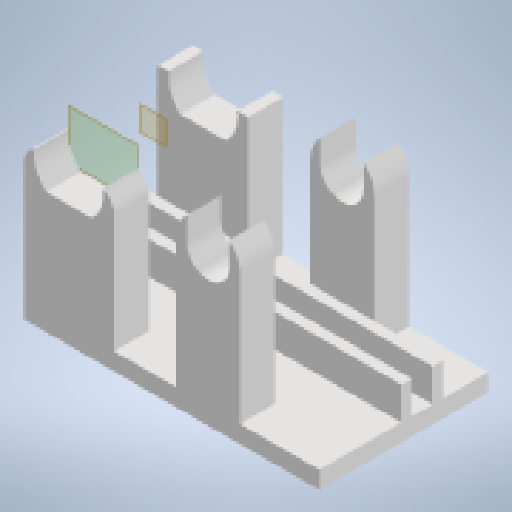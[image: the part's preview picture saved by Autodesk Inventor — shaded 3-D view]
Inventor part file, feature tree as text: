
AUTODESK INVENTOR PART (.ipt)
format: ipt  version: 2023 (Build 270158000, 158)  size: 372,224 bytes
history: native  units: mm
features: other x6, extrude x3, plane x2, sketch x2, reference x2, fillet x1, mirror x1
ambient origin geometry x8: Origin, YZ Plane, XZ Plane, XY Plane, X Axis, Y Axis, Z Axis, Center Point
bodies: Solid1 (feature_tree)
feature tree (17):
  plane  "Work Plane1"
  plane  "Work Plane2"
  sketch  "Sketch1"  dims[d0=0.1mm d1=5.0mm]
  extrude  "Extrusion1"  Depth=5.0mm
  extrude  "Extrusion2"  Depth=3.0mm
  fillet  "Fillet1"  Radius=10.0mm
  mirror  "Mirror2"
  extrude  "Extrusion3"  Depth=10.0mm TaperAngle=0.0deg
  reference  "Reference2"
  sketch  "Sketch2"  dims[d2=5.5mm d3=3.0mm d4=10.0mm d5=0.0mm d6=10.0mm d7=0.0mm d8=5.75mm d9=3.0mm d10=0.5mm d11=3.0mm d12=3.0mm d13=10.0mm d14=0.0mm]
  reference  "Reference3"
  parser-record x1  (decoder bookkeeping rows leaked as tree rows — omitted from the tree; the rows remain in map.json)
  other  "doorLockAssembly_V3.iam"
  other  "gear_V3:1"
  other  "rack_V3:1"
  other  "pinion_V3:1"
  other  "motor:2"
note: 1 file-system path scrubbed to <path> (originals preserved in map.json)
